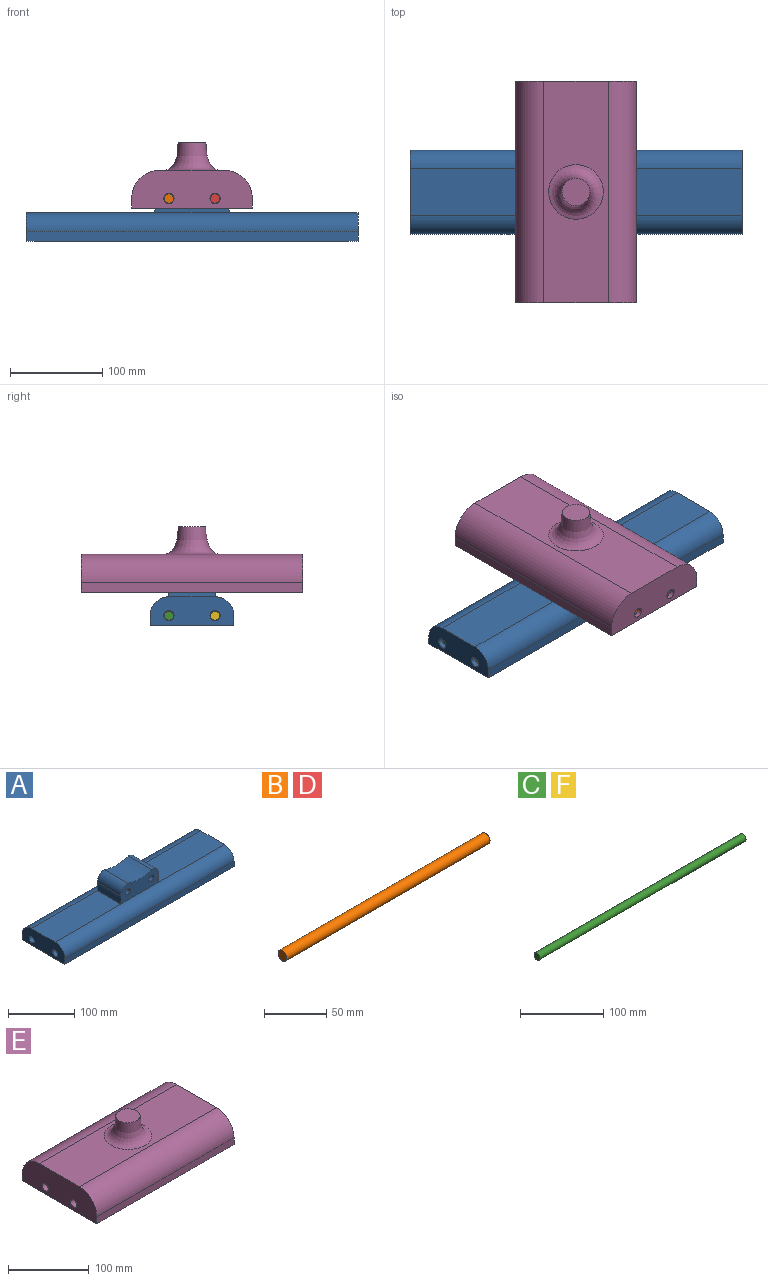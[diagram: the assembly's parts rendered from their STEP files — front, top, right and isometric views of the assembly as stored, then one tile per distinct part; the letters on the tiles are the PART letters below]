
ASSEMBLY  parts=6 mates=5
PART A: 33 faces, bbox 360x91x62 mm
  f0: plane 139.5x50mm, normal (0,0,1), area 6975mm2, adj f4,f13,f17,f25
  f1: plane 340x10.5mm, normal (0,-1,0), area 3570mm2, adj f2,f5,f9,f10
  f2: cylinder r=10.5mm len=340mm, axis (-1,0,0), area 5540mm2, adj f1,f5,f6,f7,f8,f9
  f3: plane 340x10.5mm, normal (0,1,0), area 3570mm2, adj f5,f9,f10,f15
  f4: plane 91x31mm, normal (-1,0,0), area 2450.6mm2, adj f0,f10,f13,f14,f16,f17,f22,f23
  f5: plane 71x14mm, normal (1,0,0), area 826.2mm2, adj f1,f2,f3,f6,f10,f15,f22,f23
  f6: cylinder r=7mm len=69.8mm, axis (0,1,0), area 653.4mm2, adj f2,f5,f7,f15,f22,f23
  f7: plane 326x50mm, normal (0,0,-1), area 16300mm2, adj f2,f6,f8,f15
  f8: cylinder r=7mm len=69.8mm, axis (0,1,0), area 653.4mm2, adj f2,f7,f9,f15,f19,f21
  f9: plane 71x14mm, normal (-1,0,0), area 826.2mm2, adj f1,f2,f3,f8,f10,f15,f19,f21
  f10: plane 360x91mm, normal (0,0,-1), area 8620mm2, adj f1,f3,f4,f5,f9,f11,f14,f16
  f11: plane 91x31mm, normal (1,0,0), area 2640.6mm2, adj f10,f12,f13,f14,f16,f17
  f12: plane 139.5x50mm, normal (0,0,1), area 6975mm2, adj f11,f13,f17,f26
  f13: cylinder r=20.5mm len=360mm, axis (-1,0,0), area 11592.5mm2, adj f0,f4,f11,f12,f14,f32
  f14: plane 360x10.5mm, normal (0,1,0), area 3780mm2, adj f4,f10,f11,f13
  f15: cylinder r=10.5mm len=340mm, axis (-1,0,0), area 5540mm2, adj f3,f5,f6,f7,f8,f9
  f16: plane 360x10.5mm, normal (0,-1,0), area 3780mm2, adj f4,f10,f11,f17
  f17: cylinder r=20.5mm len=360mm, axis (-1,0,0), area 11592.5mm2, adj f0,f4,f11,f12,f16,f31
  f18: plane 11x11mm, normal (-1,0,0), area 95mm2, adj f19
  f19: cylinder r=5.5mm len=11mm, axis (-1,0,0), area 174.2mm2, adj f8,f9,f18
  f20: plane 11x11mm, normal (-1,0,0), area 95mm2, adj f21
  f21: cylinder r=5.5mm len=11mm, axis (-1,0,0), area 174.2mm2, adj f8,f9,f20
  f22: cylinder r=5.5mm len=11mm, axis (-1,0,0), area 347mm2, adj f4,f5,f6
  f23: cylinder r=5.5mm len=11mm, axis (-1,0,0), area 347mm2, adj f4,f5,f6
  f24: cylinder r=15.5mm len=50mm, axis (0,1,0), area 1217.4mm2, adj f25,f29,f31,f32
  f25: cylinder r=40mm len=50mm, axis (0,1,0), area 779.9mm2, adj f0,f24,f31,f32
  f26: cylinder r=40mm len=50mm, axis (0,1,0), area 779.9mm2, adj f12,f27,f31,f32
  f27: cylinder r=15.5mm len=50mm, axis (0,1,0), area 1217.4mm2, adj f26,f29,f31,f32
  f28: cylinder r=5.5mm len=50mm, axis (0,1,0), area 1727.9mm2, adj f31,f32
  f29: cylinder r=70mm len=50mm, axis (0,1,0), area 2556.5mm2, adj f24,f27,f31,f32
  f30: cylinder r=5.5mm len=50mm, axis (0,1,0), area 1727.9mm2, adj f31,f32
  f31: plane 81x31mm, normal (0,-1,0), area 2047.2mm2, adj f17,f24,f25,f26,f27,f28,f29,f30
  f32: plane 81x31mm, normal (0,1,0), area 2047.2mm2, adj f13,f24,f25,f26,f27,f28,f29,f30
PART B: 3 faces, bbox 230x10x10 mm
  f0: cylinder r=5mm len=230mm, axis (-1,0,0), area 7225.7mm2, adj f1,f2
  f1: plane 10x10mm, normal (1,0,0), area 78.5mm2, adj f0
  f2: plane 10x10mm, normal (-1,0,0), area 78.5mm2, adj f0
PART C: 3 faces, bbox 350x10x10 mm
  f0: cylinder r=5mm len=350mm, axis (-1,0,0), area 10995.6mm2, adj f1,f2
  f1: plane 10x10mm, normal (1,0,0), area 78.5mm2, adj f0
  f2: plane 10x10mm, normal (-1,0,0), area 78.5mm2, adj f0
PART D: same geometry as B
PART E: 25 faces, bbox 240x131x71 mm
  f0: plane 220x10.5mm, normal (0,-1,0), area 2310mm2, adj f1,f6,f10,f11
  f1: cylinder r=20.5mm len=220mm, axis (-1,0,0), area 6990.7mm2, adj f0,f6,f7,f8,f9,f10
  f2: plane 220x10.5mm, normal (0,1,0), area 2310mm2, adj f6,f10,f11,f15
  f3: plane 131x41mm, normal (1,0,0), area 4971.7mm2, adj f4,f11,f12,f13,f14,f16
  f4: plane 240x70mm, normal (0,0,1), area 14044.6mm2, adj f3,f5,f12,f14,f23
  f5: plane 131x41mm, normal (-1,0,0), area 4781.7mm2, adj f4,f11,f12,f13,f14,f16,f21,f22
  f6: plane 111x24mm, normal (1,0,0), area 2430.8mm2, adj f0,f1,f2,f7,f11,f15,f21,f22
  f7: cylinder r=7mm len=100.85mm, axis (0,1,0), area 957mm2, adj f1,f6,f8,f15
  f8: plane 206x70mm, normal (0,0,-1), area 14420mm2, adj f1,f7,f9,f15
  f9: cylinder r=7mm len=100.85mm, axis (0,1,0), area 957mm2, adj f1,f8,f10,f15
  f10: plane 111x24mm, normal (-1,0,0), area 2430.8mm2, adj f0,f1,f2,f9,f11,f15,f18,f20
  f11: plane 240x131mm, normal (0,0,-1), area 7020mm2, adj f0,f2,f3,f5,f6,f10,f13,f16
  f12: cylinder r=30.5mm len=240mm, axis (-1,0,0), area 11498.2mm2, adj f3,f4,f5,f13
  f13: plane 240x10.5mm, normal (0,1,0), area 2520mm2, adj f3,f5,f11,f12
  f14: cylinder r=30.5mm len=240mm, axis (-1,0,0), area 11498.2mm2, adj f3,f4,f5,f16
  f15: cylinder r=20.5mm len=220mm, axis (-1,0,0), area 6990.7mm2, adj f2,f6,f7,f8,f9,f10
  f16: plane 240x10.5mm, normal (0,-1,0), area 2520mm2, adj f3,f5,f11,f14
  f17: plane 11x11mm, normal (-1,0,0), area 95mm2, adj f18
  f18: cylinder r=5.5mm len=11mm, axis (-1,0,0), area 172.8mm2, adj f10,f17
  f19: plane 11x11mm, normal (-1,0,0), area 95mm2, adj f20
  f20: cylinder r=5.5mm len=11mm, axis (-1,0,0), area 172.8mm2, adj f10,f19
  f21: cylinder r=5.5mm len=11mm, axis (-1,0,0), area 345.6mm2, adj f5,f6
  f22: cylinder r=5.5mm len=11mm, axis (-1,0,0), area 345.6mm2, adj f5,f6
  f23: revolved ~59.23x59.23mm, area 4348.6mm2, adj f4,f24
  f24: plane 30x30mm, normal (0,0,1), area 706.9mm2, adj f23
PART F: same geometry as C
PLACE A t=(-61.93,-89.17,-14.97)mm
PLACE B rot(axis=(0,0,1),90deg) t=(-86.93,-89.17,21.03)mm fixed
PLACE C t=(-61.93,-27.98,-14.97)mm
PLACE D rot(axis=(0,0,1),90deg) t=(-36.93,-89.17,21.03)mm
PLACE E rot(axis=(0,0,1),90deg) t=(-61.93,-89.17,21.03)mm
PLACE F t=(-61.93,-77.98,-14.97)mm
MATE fastened D.f0 <-> E.f18  axis (0,1,0) through (-36.93,25.83,21.03)mm
MATE fastened E.f20 <-> B.f0  axis (0,-1,0) through (-86.93,25.83,21.03)mm
MATE slider A.f24 <-> B.f0  axis (0,1,0) through (-86.93,-89.17,21.03)mm
MATE fastened F.f0 <-> A.f19  axis (1,0,0) through (113.07,-114.17,-14.97)mm
MATE fastened A.f13 <-> C.f0  axis (-1,0,0) through (113.07,-64.17,-14.97)mm
